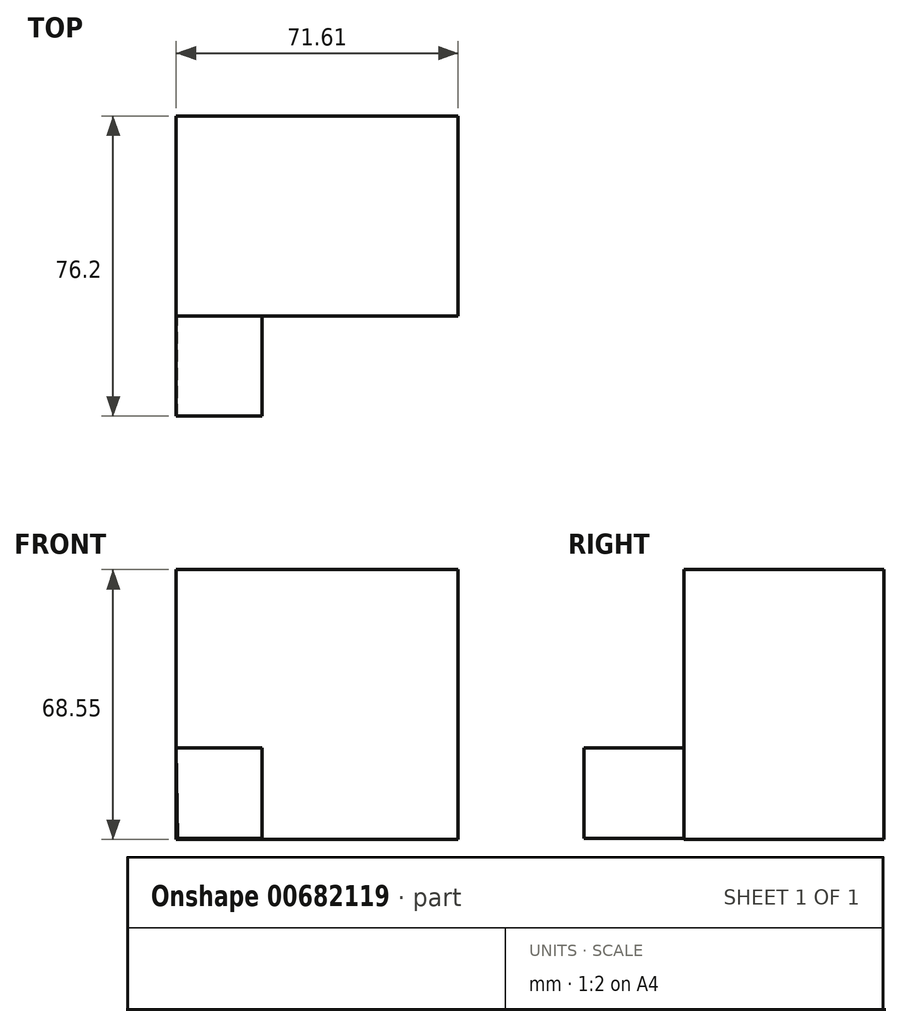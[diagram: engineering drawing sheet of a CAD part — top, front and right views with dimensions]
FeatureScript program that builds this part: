
annotation { "Feature Type Name" : "Feature", "Feature Type Description" : "" }
export const myFeature = defineFeature(function(context is Context, id is Id, definition is map)
    precondition{}
    {
        {
            var Q0;
            Q0=qCreatedBy(makeId("Front.planeOp"),FACE);
            var sketch = newSketch(context, id + "F0", { "sketchPlane" : qUnion([Q0])});
            skLineSegment(sketch, "E0", {"start": v(-39.05, 40.39) * mm, "end": v(-39.05, -29.12) * mm});
            skLineSegment(sketch, "E1", {"start": v(-39.05, -29.12) * mm, "end": v(32.56, -29.12) * mm});
            skLineSegment(sketch, "E2", {"start": v(32.56, -29.12) * mm, "end": v(32.56, 39.43) * mm});
            skLineSegment(sketch, "E3", {"start": v(32.56, 39.43) * mm, "end": v(-39.05, 39.43) * mm});
            skSolve(sketch);
        }
        {
            var Q0;
            Q0 = qSketchRegion(id + "F0", true);
            extrude(context, id + "F1", {"entities" : qUnion([Q0]), "depth" : 50.8 * mm, "offsetDistance" : 25.4 * mm});
        }
        {
            var Q0;
            Q0=makeQuery(id+"F1.opExtrude","CAP_FACE",FACE,{"disambiguationData":[OSD([sQuery(id+"F0.wireOp",EDGE,"E0"),sQuery(id+"F0.wireOp",EDGE,"E1"),sQuery(id+"F0.wireOp",EDGE,"E2"),sQuery(id+"F0.wireOp",EDGE,"E3")])],"isStart":false});
            var sketch = newSketch(context, id + "F2", { "sketchPlane" : qUnion([Q0])});
            skLineSegment(sketch, "E4", {"start": v(-39.05, -5.26) * mm, "end": v(-17.33, -5.26) * mm});
            skLineSegment(sketch, "E5", {"start": v(-17.33, -5.26) * mm, "end": v(-17.33, -29.12) * mm});
            skLineSegment(sketch, "E6", {"start": v(-17.33, -29.12) * mm, "end": v(-39.05, -29.12) * mm});
            skLineSegment(sketch, "E7", {"start": v(-39.05, -29.12) * mm, "end": v(-39.05, -5.26) * mm});
            skSolve(sketch);
        }
        {
            var Q0;
            {var subQ2=sQuery(id+"F2.wireOp",EDGE,"E4");Q0=makeQuery(id+"F2.imprint","IMPRINT",FACE,{"disambiguationData":[TD([[makeQuery(id+"F2.imprint","IMPRINT",EDGE,{"derivedFrom":subQ2}),1.0]])]});}
            var sketch = newSketch(context, id + "F3", { "sketchPlane" : qUnion([Q0])});
            skLineSegment(sketch, "E8", {"start": v(-38.67, -28.93) * mm, "end": v(-17.28, -28.93) * mm});
            skLineSegment(sketch, "E9", {"start": v(-17.28, -28.93) * mm, "end": v(-17.28, -5.82) * mm});
            skLineSegment(sketch, "E10", {"start": v(-17.28, -5.82) * mm, "end": v(-39.05, -5.82) * mm});
            skLineSegment(sketch, "E11", {"start": v(-39.05, -5.82) * mm, "end": v(-38.67, -28.93) * mm});
            skSolve(sketch);
        }
        {
            var Q0;
            Q0 = qSketchRegion(id + "F3", true);
            extrude(context, id + "F4", {"entities" : qUnion([Q0]), "operationType" : NewBodyOperationType.ADD, "depth" : 25.4 * mm, "offsetDistance" : 25.4 * mm});
        }
    });
